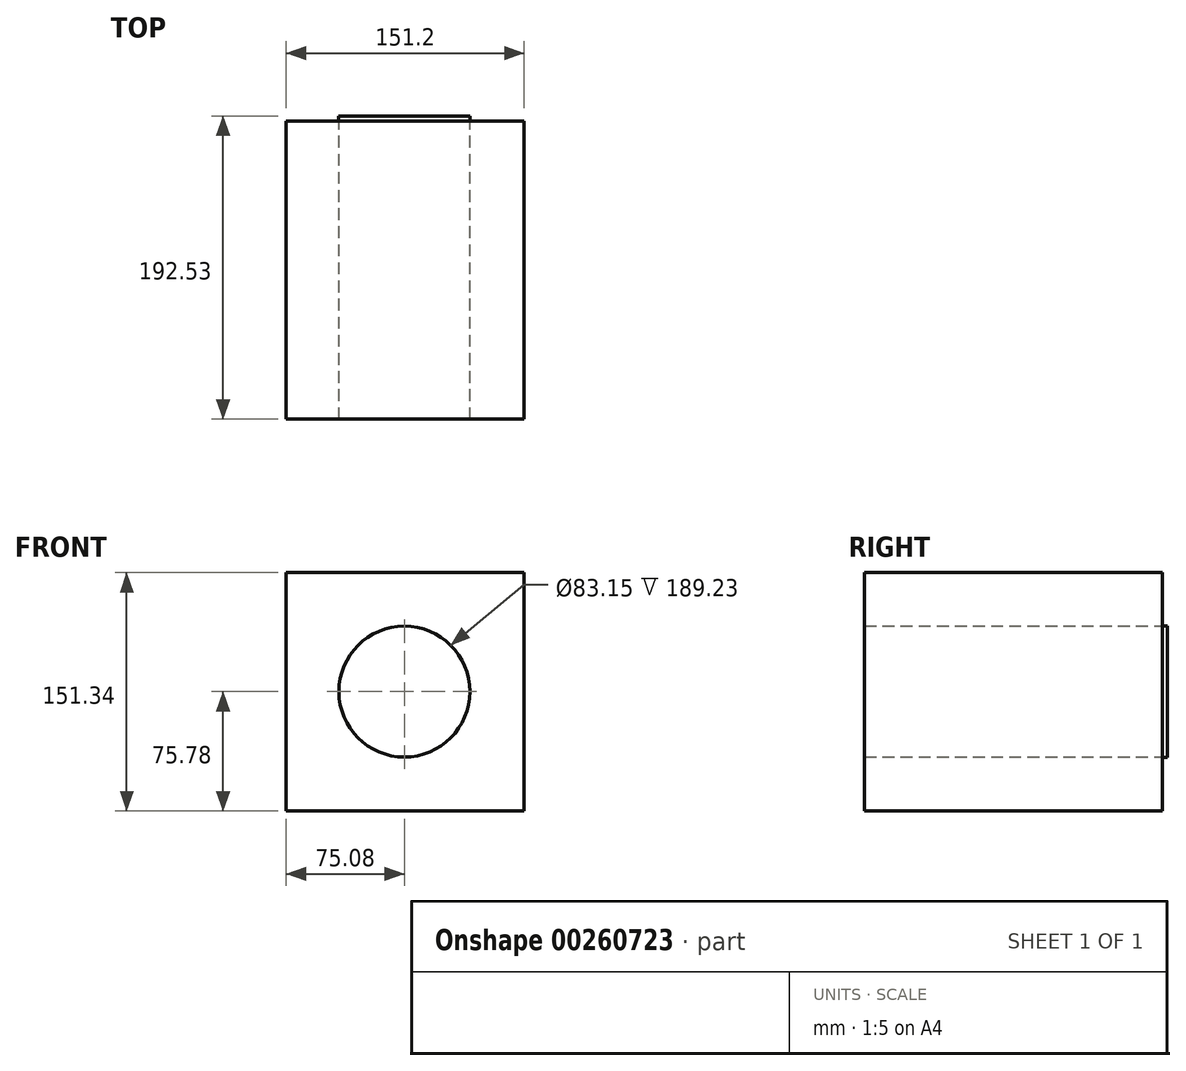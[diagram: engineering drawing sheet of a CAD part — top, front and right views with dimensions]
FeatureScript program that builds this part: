
annotation { "Feature Type Name" : "Feature", "Feature Type Description" : "" }
export const myFeature = defineFeature(function(context is Context, id is Id, definition is map)
    precondition{}
    {
        {
            var Q0;
            Q0=qCreatedBy(makeId("Front.planeOp"),FACE);
            var sketch = newSketch(context, id + "F0", { "sketchPlane" : qUnion([Q0])});
            skLineSegment(sketch, "E0.bottom", {"start": v(-75.08, 75.56) * mm, "end": v(76.12, 75.56) * mm});
            skLineSegment(sketch, "E0.top", {"start": v(-75.08, -75.78) * mm, "end": v(76.12, -75.78) * mm});
            skLineSegment(sketch, "E0.left", {"start": v(-75.08, 75.56) * mm, "end": v(-75.08, -75.78) * mm});
            skLineSegment(sketch, "E0.right", {"start": v(76.12, 75.56) * mm, "end": v(76.12, -75.78) * mm});
            skCircle(sketch, "E1", {"center": v(0, 0) * mm, "radius": 41.58 * mm});
            skSolve(sketch);
        }
        {
            var Q0;
            Q0 = qSketchRegion(id + "F0", true);
            extrude(context, id + "F1", {"entities" : qUnion([Q0]), "depth" : 189.23 * mm});
        }
        {
            var Q0;
            Q0=makeQuery(id+"F1.opExtrude","CAP_FACE",FACE,{"disambiguationData":[OSD([sQuery(id+"F0.wireOp",EDGE,"E0.bottom"),sQuery(id+"F0.wireOp",EDGE,"E0.top"),sQuery(id+"F0.wireOp",EDGE,"E0.left"),sQuery(id+"F0.wireOp",EDGE,"E0.right"),sQuery(id+"F0.wireOp",EDGE,"E1")])],"isStart":true});
            var sketch = newSketch(context, id + "F2", { "sketchPlane" : qUnion([Q0])});
            skSolve(sketch);
        }
        {
            var Q0;
            Q0=makeQuery(id+"F2.imprint","IMPRINT",FACE,{"disambiguationData":[TD([[makeQuery(id+"F2.imprint","IMPRINT",EDGE,{"derivedFrom":makeQuery(id+"F1.opExtrude","CAP_EDGE",EDGE,{"disambiguationData":[OSD([sQuery(id+"F0.wireOp",EDGE,"E1")])],"isStart":true})}),-1.0]])]});
            var sketch = newSketch(context, id + "F3", { "sketchPlane" : qUnion([Q0])});
            skCircle(sketch, "E2", {"center": v(0, 0) * mm, "radius": 41.74 * mm});
            skSolve(sketch);
        }
        {
            var Q0;
            Q0 = qSketchRegion(id + "F3", true);
            extrude(context, id + "F4", {"entities" : qUnion([Q0]), "operationType" : NewBodyOperationType.ADD, "depth" : 3.3 * mm});
        }
    });
